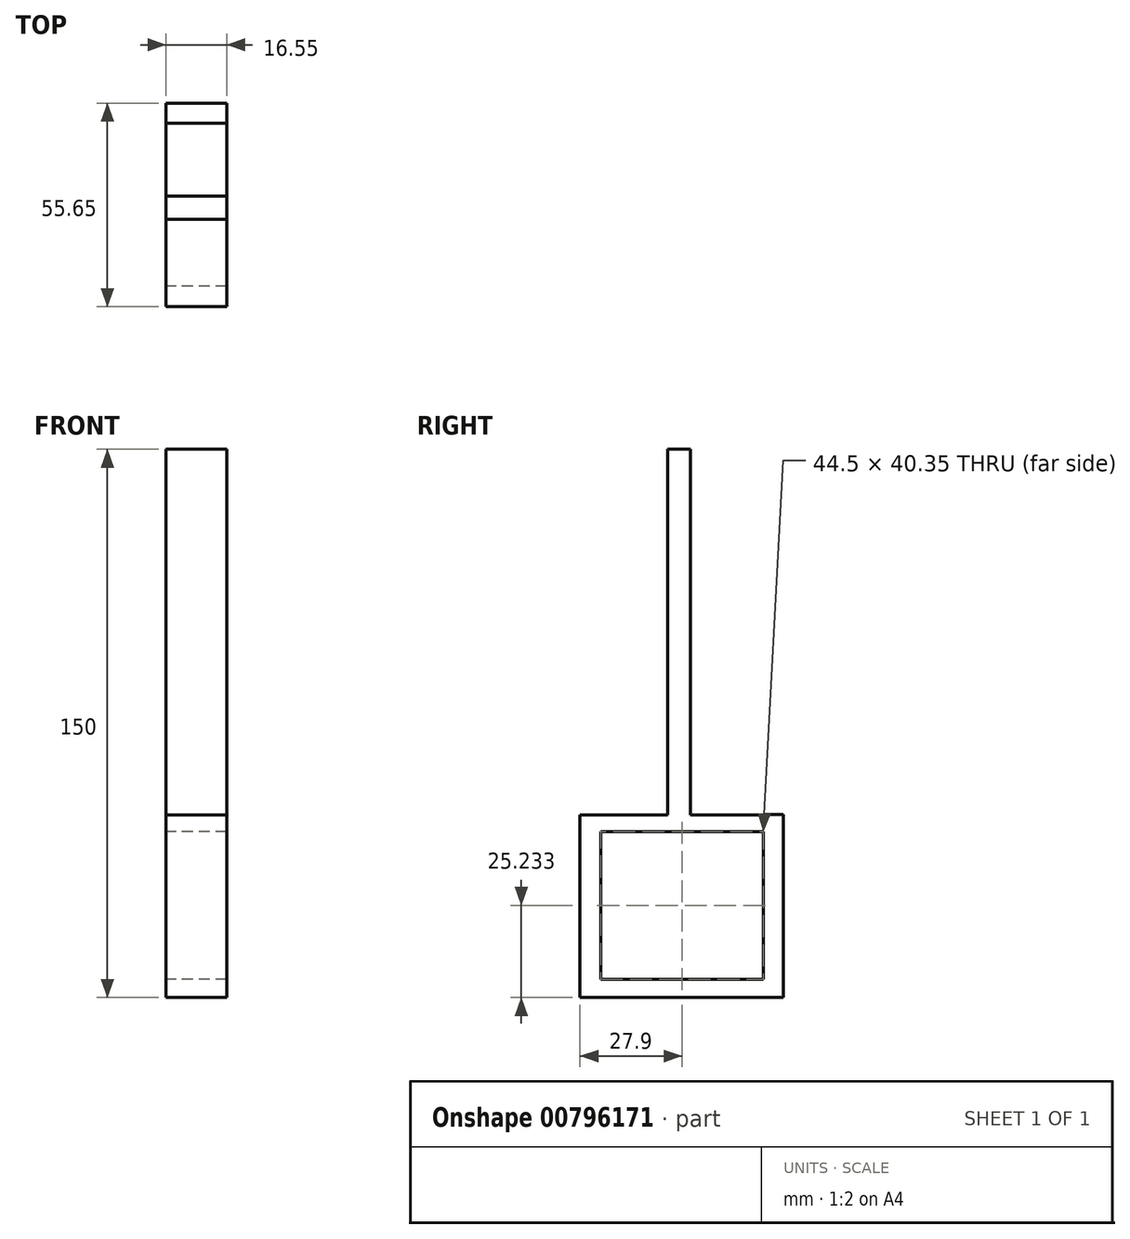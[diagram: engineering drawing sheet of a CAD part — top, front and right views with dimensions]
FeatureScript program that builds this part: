
annotation { "Feature Type Name" : "Feature", "Feature Type Description" : "" }
export const myFeature = defineFeature(function(context is Context, id is Id, definition is map)
    precondition{}
    {
        {
            var Q0;
            Q0=qCreatedBy(makeId("Top.planeOp"),FACE);
            var sketch = newSketch(context, id + "F0", { "sketchPlane" : qUnion([Q0])});
            skLineSegment(sketch, "E0.bottom", {"start": v(0, 0) * mm, "end": v(-16.55, 0) * mm});
            skLineSegment(sketch, "E0.top", {"start": v(0, 5.65) * mm, "end": v(-16.55, 5.65) * mm});
            skLineSegment(sketch, "E0.left", {"start": v(0, 0) * mm, "end": v(0, 5.65) * mm});
            skLineSegment(sketch, "E0.right", {"start": v(-16.55, 0) * mm, "end": v(-16.55, 5.65) * mm});
            skSolve(sketch);
        }
        {
            var Q0;
            Q0=makeQuery(id+"F0.imprint","IMPRINT",FACE,{"disambiguationData":[TD([[makeQuery(id+"F0.imprint","IMPRINT",EDGE,{"derivedFrom":sQuery(id+"F0.wireOp",EDGE,"E0.bottom")}),-1.0]])]});
            extrude(context, id + "F1", {"entities" : qUnion([Q0]), "depth" : 50 * mm, "offsetDistance" : 25 * mm});
        }
        {
            var Q0;
            Q0=makeQuery(id+"F1.opExtrude","SWEPT_FACE",FACE,{"disambiguationData":[OSD([sQuery(id+"F0.wireOp",EDGE,"E0.top")])]});
            var sketch = newSketch(context, id + "F2", { "sketchPlane" : qUnion([Q0])});
            skLineSegment(sketch, "E1.bottom", {"start": v(0, 45.4) * mm, "end": v(16.55, 45.4) * mm});
            skLineSegment(sketch, "E1.top", {"start": v(0, 50) * mm, "end": v(16.55, 50) * mm});
            skLineSegment(sketch, "E1.left", {"start": v(0, 45.4) * mm, "end": v(0, 50) * mm});
            skLineSegment(sketch, "E1.right", {"start": v(16.55, 45.4) * mm, "end": v(16.55, 50) * mm});
            skSolve(sketch);
        }
        {
            var Q0;
            Q0=makeQuery(id+"F2.imprint","IMPRINT",FACE,{"disambiguationData":[TD([[makeQuery(id+"F2.imprint","IMPRINT",EDGE,{"derivedFrom":sQuery(id+"F2.wireOp",EDGE,"E1.bottom")}),1.0]])]});
            extrude(context, id + "F3", {"entities" : qUnion([Q0]), "operationType" : NewBodyOperationType.ADD, "depth" : 50 * mm, "offsetDistance" : 25 * mm});
        }
        {
            var Q0;
            Q0=makeQuery(id+"F1.opExtrude","SWEPT_FACE",FACE,{"disambiguationData":[OSD([sQuery(id+"F0.wireOp",EDGE,"E0.top")])]});
            var sketch = newSketch(context, id + "F4", { "sketchPlane" : qUnion([Q0])});
            skLineSegment(sketch, "E2.bottom", {"start": v(0, 0) * mm, "end": v(16.55, 0) * mm});
            skLineSegment(sketch, "E2.top", {"start": v(0, 5.06) * mm, "end": v(16.55, 5.06) * mm});
            skLineSegment(sketch, "E2.left", {"start": v(0, 0) * mm, "end": v(0, 5.06) * mm});
            skLineSegment(sketch, "E2.right", {"start": v(16.55, 0) * mm, "end": v(16.55, 5.06) * mm});
            skSolve(sketch);
        }
        {
            var Q0;
            Q0=makeQuery(id+"F4.imprint","IMPRINT",FACE,{"disambiguationData":[TD([[makeQuery(id+"F4.imprint","IMPRINT",EDGE,{"derivedFrom":sQuery(id+"F4.wireOp",EDGE,"E2.bottom")}),1.0]])]});
            extrude(context, id + "F5", {"entities" : qUnion([Q0]), "operationType" : NewBodyOperationType.ADD, "depth" : 50 * mm, "offsetDistance" : 25 * mm});
        }
        {
            var Q0;
            Q0=makeQuery(id+"F5.opExtrude","SWEPT_FACE",FACE,{"disambiguationData":[OSD([sQuery(id+"F4.wireOp",EDGE,"E2.top")])]});
            var sketch = newSketch(context, id + "F6", { "sketchPlane" : qUnion([Q0])});
            skLineSegment(sketch, "E3.bottom", {"start": v(-16.55, 55.65) * mm, "end": v(0, 55.65) * mm});
            skLineSegment(sketch, "E3.top", {"start": v(-16.55, 50.15) * mm, "end": v(0, 50.15) * mm});
            skLineSegment(sketch, "E3.left", {"start": v(-16.55, 55.65) * mm, "end": v(-16.55, 50.15) * mm});
            skLineSegment(sketch, "E3.right", {"start": v(0, 55.65) * mm, "end": v(0, 50.15) * mm});
            skSolve(sketch);
        }
        {
            var Q0;
            Q0=makeQuery(id+"F6.imprint","IMPRINT",FACE,{"disambiguationData":[TD([[makeQuery(id+"F6.imprint","IMPRINT",EDGE,{"derivedFrom":sQuery(id+"F6.wireOp",EDGE,"E3.bottom")}),1.0]])]});
            extrude(context, id + "F7", {"entities" : qUnion([Q0]), "operationType" : NewBodyOperationType.ADD, "depth" : 45 * mm, "offsetDistance" : 25 * mm});
        }
        {
            var Q0;
            Q0=makeQuery(id+"F3.boolean.opBoolean","MERGE",FACE,{"derivedFrom":[makeQuery(id+"F1.opExtrude","CAP_FACE",FACE,{"disambiguationData":[OSD([sQuery(id+"F0.wireOp",EDGE,"E0.bottom"),sQuery(id+"F0.wireOp",EDGE,"E0.top"),sQuery(id+"F0.wireOp",EDGE,"E0.left"),sQuery(id+"F0.wireOp",EDGE,"E0.right")])],"isStart":false}),makeQuery(id+"F3.opExtrude","SWEPT_FACE",FACE,{"disambiguationData":[OSD([sQuery(id+"F2.wireOp",EDGE,"E1.top")])]})]});
            var sketch = newSketch(context, id + "F8", { "sketchPlane" : qUnion([Q0])});
            skLineSegment(sketch, "E4.bottom", {"start": v(-16.55, 30.2) * mm, "end": v(0, 30.2) * mm});
            skLineSegment(sketch, "E4.top", {"start": v(-16.55, 23.93) * mm, "end": v(0, 23.93) * mm});
            skLineSegment(sketch, "E4.left", {"start": v(-16.55, 30.2) * mm, "end": v(-16.55, 23.93) * mm});
            skLineSegment(sketch, "E4.right", {"start": v(0, 30.2) * mm, "end": v(0, 23.93) * mm});
            skSolve(sketch);
        }
        {
            var Q0;
            Q0=makeQuery(id+"F8.imprint","IMPRINT",FACE,{"disambiguationData":[TD([[makeQuery(id+"F8.imprint","IMPRINT",EDGE,{"derivedFrom":sQuery(id+"F8.wireOp",EDGE,"E4.bottom")}),-1.0]])]});
            extrude(context, id + "F9", {"entities" : qUnion([Q0]), "operationType" : NewBodyOperationType.ADD, "depth" : 100 * mm, "offsetDistance" : 25 * mm});
        }
    });
